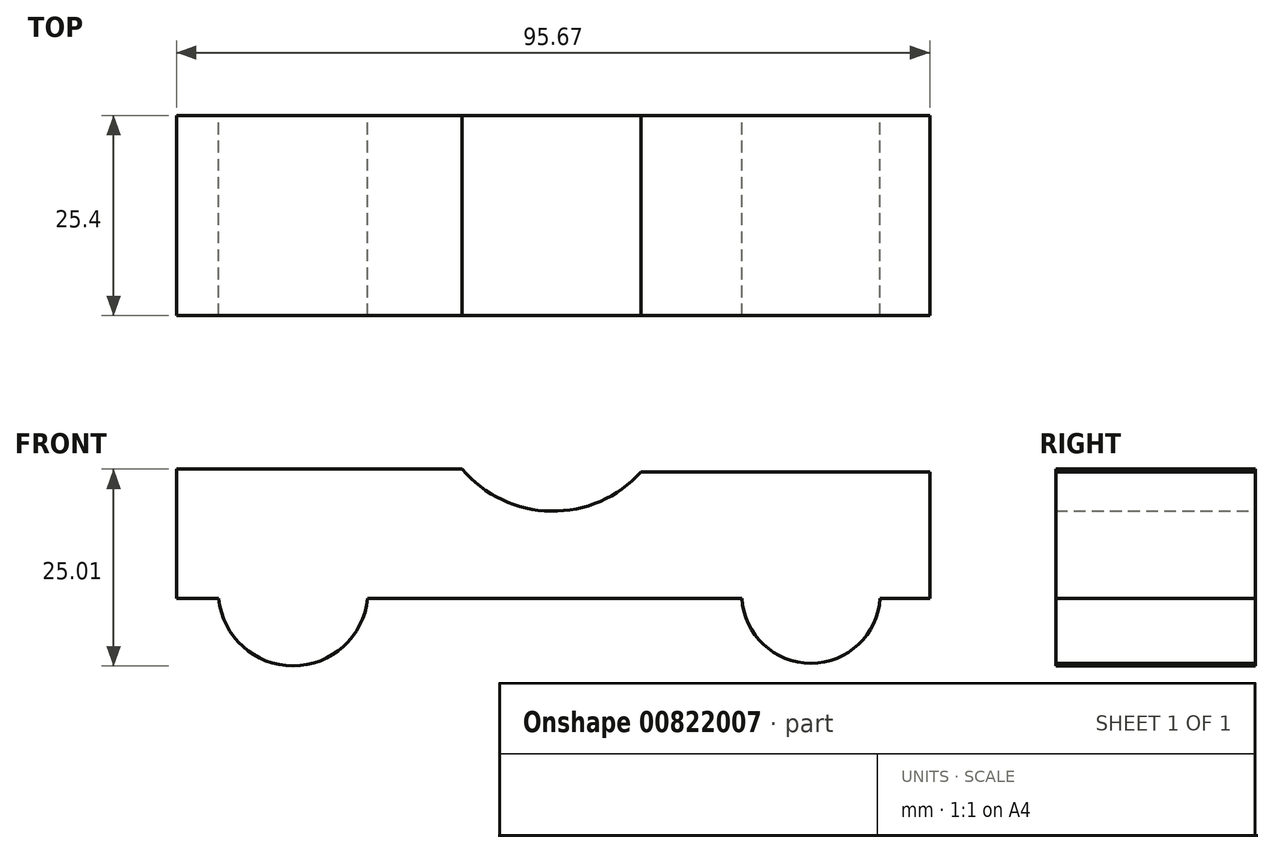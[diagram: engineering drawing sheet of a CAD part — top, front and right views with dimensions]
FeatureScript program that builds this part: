
annotation { "Feature Type Name" : "Feature", "Feature Type Description" : "" }
export const myFeature = defineFeature(function(context is Context, id is Id, definition is map)
    precondition{}
    {
        {
            var Q0;
            Q0=qCreatedBy(makeId("Front.planeOp"),FACE);
            var sketch = newSketch(context, id + "F0", { "sketchPlane" : qUnion([Q0])});
            skLineSegment(sketch, "E0", {"start": v(47.45, 6.78) * mm, "end": v(47.45, -9.26) * mm});
            skLineSegment(sketch, "E1", {"start": v(47.45, -9.26) * mm, "end": v(41.15, -9.26) * mm});
            skLineSegment(sketch, "E2", {"start": v(-48.22, -9.26) * mm, "end": v(-48.22, 7.16) * mm});
            skLineSegment(sketch, "E3", {"start": v(-48.22, 7.16) * mm, "end": v(-17.66, 7.16) * mm});
            skLineSegment(sketch, "E4", {"start": v(47.45, 6.78) * mm, "end": v(16.52, 6.78) * mm});
            skLineSegment(sketch, "E5", {"start": v(-17.66, 7.16) * mm, "end": v(-11.93, 7.16) * mm});
            skLineSegment(sketch, "E6", {"start": v(16.52, 6.78) * mm, "end": v(10.79, 6.78) * mm});
            skPoint(sketch, "E7.start.orphan", {"position": v(10.79, 31.98) * mm});
            skArc(sketch, "E8", {"start": v(-11.93, 7.16) * mm, "mid": v(-0.66, 1.8) * mm, "end": v(10.79, 6.78) * mm});
            skArc(sketch, "E9", {"start": v(41.15, -9.26) * mm, "mid": v(32.37, -4.29) * mm, "end": v(23.58, -9.26) * mm});
            skArc(sketch, "E10", {"start": v(-23.96, -9.26) * mm, "mid": v(-33.42, -4.03) * mm, "end": v(-42.87, -9.26) * mm});
            skLineSegment(sketch, "E11.trimOffspring", {"start": v(-42.87, -9.26) * mm, "end": v(-48.22, -9.26) * mm});
            skArc(sketch, "E12", {"start": v(-42.87, -9.26) * mm, "mid": v(-33.42, -17.85) * mm, "end": v(-23.96, -9.26) * mm});
            skArc(sketch, "E13", {"start": v(23.58, -9.26) * mm, "mid": v(32.37, -17.5) * mm, "end": v(41.15, -9.26) * mm});
            skLineSegment(sketch, "E14.trimOffspring", {"start": v(23.58, -9.26) * mm, "end": v(-23.96, -9.26) * mm});
            skSolve(sketch);
        }
        {
            var Q0;
            Q0 = qSketchRegion(id + "F0", true);
            extrude(context, id + "F1", {"entities" : qUnion([Q0]), "depth" : 25.4 * mm, "offsetDistance" : 25.4 * mm});
        }
    });
